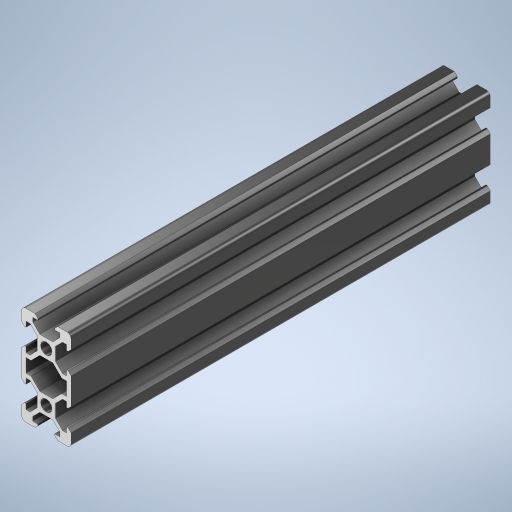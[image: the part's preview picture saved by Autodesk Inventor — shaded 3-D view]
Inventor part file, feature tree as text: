
AUTODESK INVENTOR PART (.ipt)
format: ipt  version: 2024.2 (Build 282272000, 272)  size: 641,536 bytes
history: native  units: mm
features: extrude x2, mirror x2, pattern_circular x1, chamfer x1, plane x1, fillet x1, sketch x1, other x1, projected_geometry x1
ambient origin geometry x8: Origin, YZ Plane, XZ Plane, XY Plane, X Axis, Y Axis, Z Axis, Center Point
bodies: Solid1 (feature_tree)
feature tree (11):
  extrude  "Extrusion1"  TaperAngle=135.0deg  [1 undecoded]
  pattern_circular  "Circular Pattern1"  Count=2  [1 undecoded]
  chamfer  "Chamfer1"  Distance=170.0mm
  plane  "Work Plane1"
  mirror  "Mirror1"
  extrude  "Extrusion2"  Depth=40.0mm TaperAngle=360.0deg
  fillet  "Fillet2"  Radius=11.0mm
  mirror  "Mirror2"
  sketch  "Sketch1"  dims[d0=1.5mm d6=6.3mm d9=4.6mm d18=135.0deg d22=20.0mm d24=170.0mm d25=0.0mm d26=40.0mm d27=360.0deg d34=11.0mm d35=6.79mm d36=1.8mm d37=1.185mm d38=2.0mm d39=45.0deg d42=1.8mm d43=0.0mm d44=0.0mm d45=1.5mm d46=0.5mm d47=0.872665mm d48=0.5mm d49=0.872665mm]
  other  "Image1"
  projected_geometry  "Projected Loop1"
note: 2 required parameter values undecoded (feature->parameter linkage not recoverable at this tier; creation-order binding heuristic only, values carry confidence <= 0.55)
